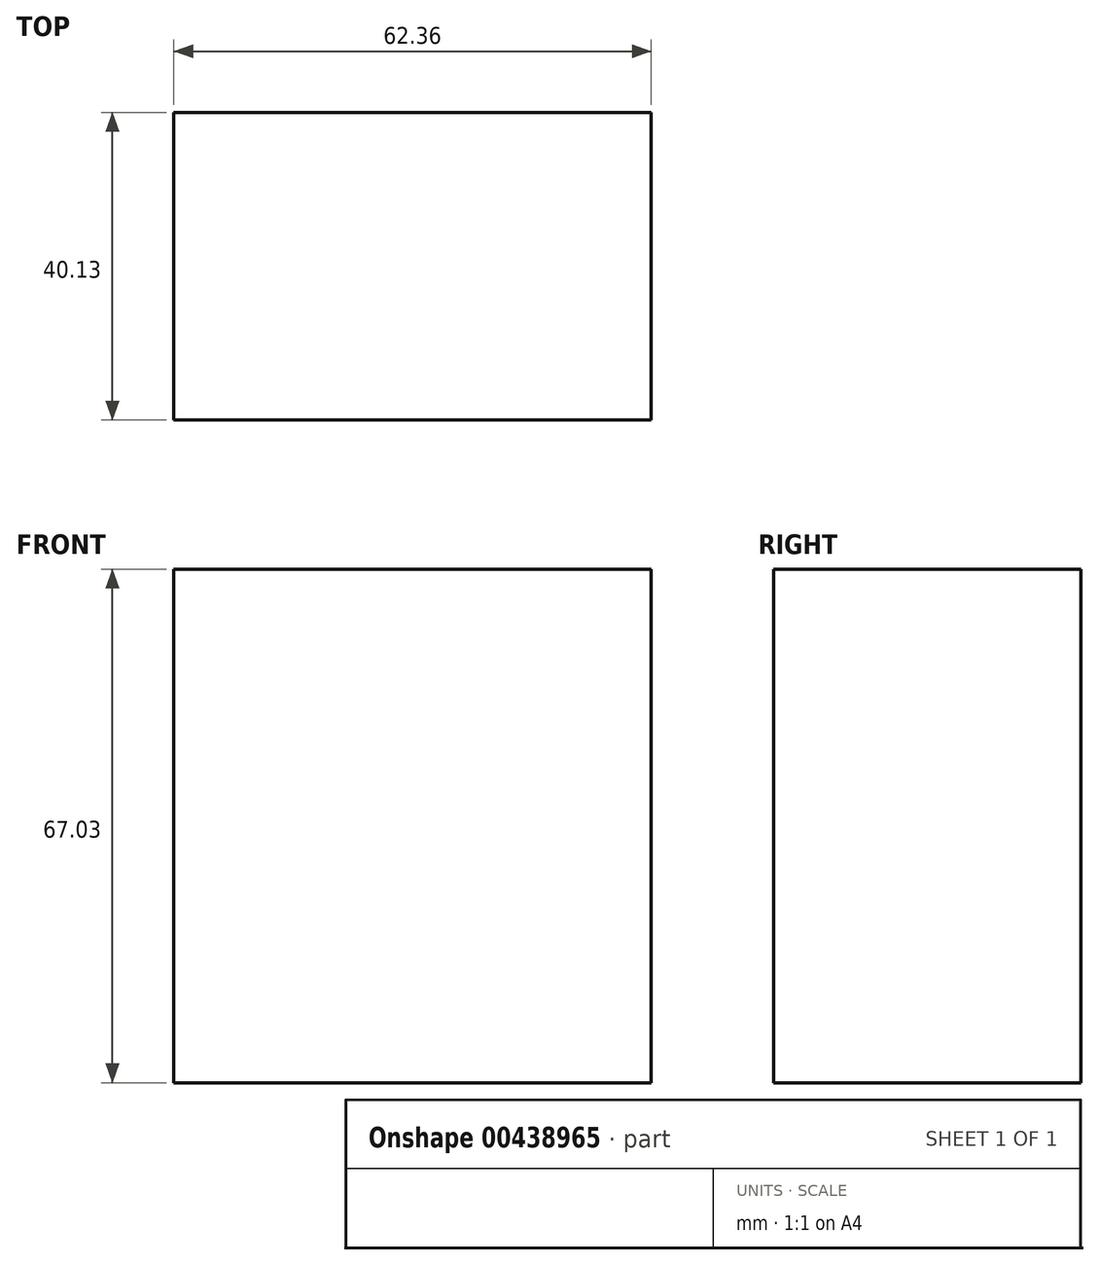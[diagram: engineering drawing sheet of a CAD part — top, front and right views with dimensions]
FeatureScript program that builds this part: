
annotation { "Feature Type Name" : "Feature", "Feature Type Description" : "" }
export const myFeature = defineFeature(function(context is Context, id is Id, definition is map)
    precondition{}
    {
        {
            var Q0;
            Q0=qCreatedBy(makeId("Front.planeOp"),FACE);
            var sketch = newSketch(context, id + "F0", { "sketchPlane" : qUnion([Q0])});
            skLineSegment(sketch, "E0.bottom", {"start": v(0, 0) * mm, "end": v(62.36, 0) * mm});
            skLineSegment(sketch, "E0.top", {"start": v(0, 67.03) * mm, "end": v(62.36, 67.03) * mm});
            skLineSegment(sketch, "E0.left", {"start": v(0, 0) * mm, "end": v(0, 67.03) * mm});
            skLineSegment(sketch, "E0.right", {"start": v(62.36, 0) * mm, "end": v(62.36, 67.03) * mm});
            skSolve(sketch);
        }
        {
            var Q0;
            Q0=makeQuery(id+"F0.imprint","IMPRINT",FACE,{"disambiguationData":[TD([[makeQuery(id+"F0.imprint","IMPRINT",EDGE,{"derivedFrom":sQuery(id+"F0.wireOp",EDGE,"E0.bottom")}),1.0]])]});
            extrude(context, id + "F1", {"entities" : qUnion([Q0]), "depth" : 40.13 * mm});
        }
    });
